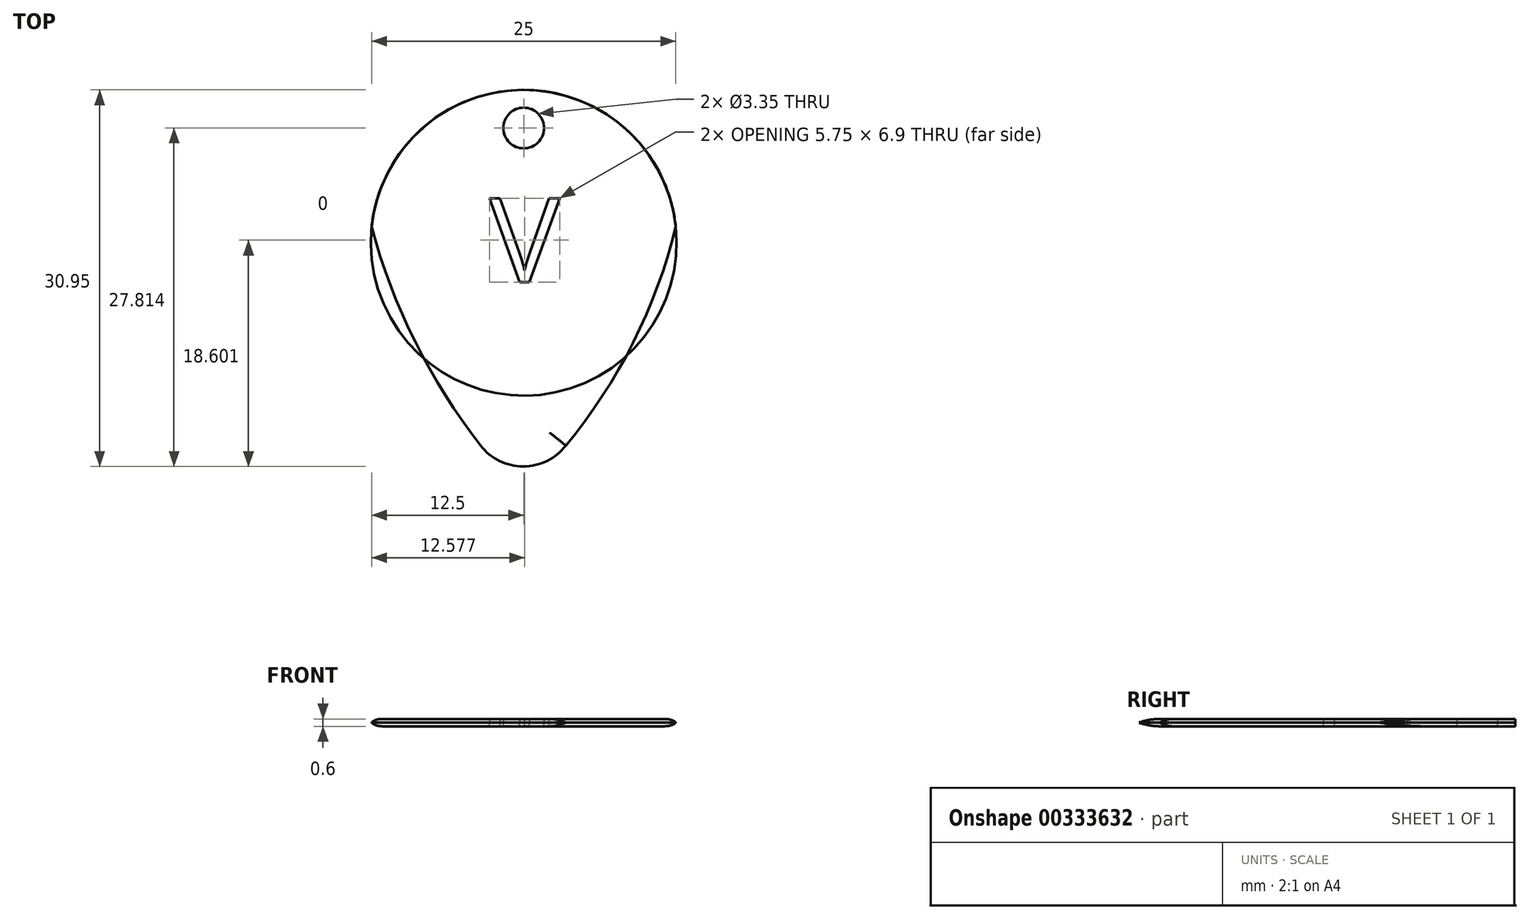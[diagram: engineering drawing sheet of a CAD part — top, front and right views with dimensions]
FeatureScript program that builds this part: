
annotation { "Feature Type Name" : "Feature", "Feature Type Description" : "" }
export const myFeature = defineFeature(function(context is Context, id is Id, definition is map)
    precondition{}
    {
        {
            var Q0;
            Q0=qCreatedBy(makeId("Top.planeOp"),FACE);
            var sketch = newSketch(context, id + "F0", { "sketchPlane" : qUnion([Q0])});
            skArc(sketch, "E0", {"start": v(12.5, 4.52) * mm, "mid": v(0, 15.8) * mm, "end": v(-12.5, 4.52) * mm});
            skArc(sketch, "E1", {"start": v(-3.54, -13.43) * mm, "mid": v(-0.04, -15.15) * mm, "end": v(3.46, -13.43) * mm});
            skArc(sketch, "E2", {"start": v(-12.5, 4.52) * mm, "mid": v(-8.92, -4.9) * mm, "end": v(-3.54, -13.43) * mm});
            skArc(sketch, "E3", {"start": v(3.46, -13.43) * mm, "mid": v(9, -4.96) * mm, "end": v(12.5, 4.52) * mm});
            skCircle(sketch, "E4", {"center": v(0, 12.66) * mm, "radius": 1.67 * mm});
            skText(sketch, "E5", { "text": "V", "fontName": "OpenSans-Regular.ttf"});
            const initialGuessF0  = {"E5": [-0.0028, 0, 1, 0, 0.00696]};
            skSetInitialGuess(sketch, initialGuessF0);
            skSolve(sketch);
        }
        {
            var Q0;
            Q0=makeQuery(id+"F0.imprint","IMPRINT",FACE,{"disambiguationData":[TD([[makeQuery(id+"F0.imprint","IMPRINT",EDGE,{"derivedFrom":sQuery(id+"F0.wireOp",EDGE,"E0")}),1.0]])]});
            extrude(context, id + "F1", {"entities" : qUnion([Q0]), "depth" : .3 * mm});
        }
        {
            var Q0;
            Q0=makeQuery(id+"F1.opExtrude","CAP_EDGE",EDGE,{"disambiguationData":[OSD([sQuery(id+"F0.wireOp",EDGE,"E3")])],"isStart":false});
            var Q1;
            Q1=makeQuery(id+"F1.opExtrude","CAP_EDGE",EDGE,{"disambiguationData":[OSD([sQuery(id+"F0.wireOp",EDGE,"E1")])],"isStart":false});
            var Q2;
            Q2=makeQuery(id+"F1.opExtrude","CAP_EDGE",EDGE,{"disambiguationData":[OSD([sQuery(id+"F0.wireOp",EDGE,"E2")])],"isStart":false});
            fillet(context, id + "F2", {"entities" : qUnion([Q0, Q1, Q2]), "radius" : 5 * mm, "tangentPropagation" : true, "allowEdgeOverflow" : false});
        }
        {
            var Q0;
            Q0=makeQuery(id+"F1.opExtrude","SWEPT_BODY",BODY,{"disambiguationData":[OSD([sQuery(id+"F0.wireOp",EDGE,"E0"),sQuery(id+"F0.wireOp",EDGE,"E1"),sQuery(id+"F0.wireOp",EDGE,"E2"),sQuery(id+"F0.wireOp",EDGE,"E3"),sQuery(id+"F0.wireOp",EDGE,"E4"),sQuery(id+"F0.wireOp",EDGE,"E5.sketch_text.stroke-0"),sQuery(id+"F0.wireOp",EDGE,"E5.sketch_text.stroke-1"),sQuery(id+"F0.wireOp",EDGE,"E5.sketch_text.stroke-2"),sQuery(id+"F0.wireOp",EDGE,"E5.sketch_text.stroke-3"),sQuery(id+"F0.wireOp",EDGE,"E5.sketch_text.stroke-4"),sQuery(id+"F0.wireOp",EDGE,"E5.sketch_text.stroke-5"),sQuery(id+"F0.wireOp",EDGE,"E5.sketch_text.stroke-6"),sQuery(id+"F0.wireOp",EDGE,"E5.sketch_text.stroke-7"),sQuery(id+"F0.wireOp",EDGE,"E5.sketch_text.stroke-8")])]});
            var Q1;
            Q1=qCreatedBy(makeId("Top.planeOp"),FACE);
            mirror(context, id + "F3", {"entities" : qUnion([Q0]), "mirrorPlane" : qUnion([Q1])});
        }
    });
